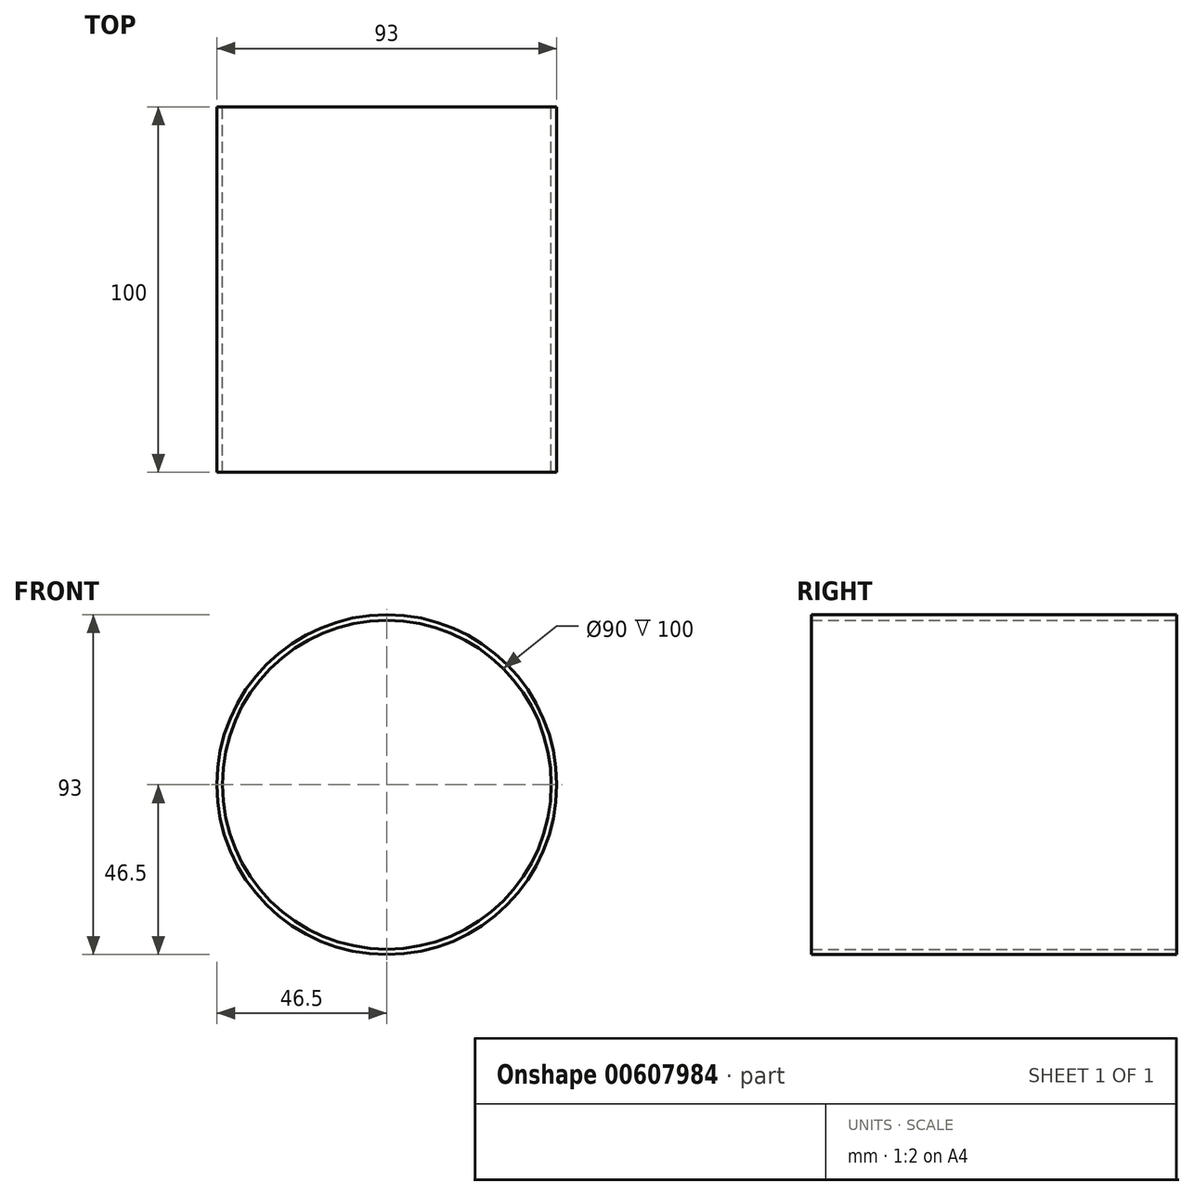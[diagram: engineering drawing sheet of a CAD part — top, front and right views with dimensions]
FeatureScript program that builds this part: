
annotation { "Feature Type Name" : "Feature", "Feature Type Description" : "" }
export const myFeature = defineFeature(function(context is Context, id is Id, definition is map)
    precondition{}
    {
        {
            var Q0;
            Q0=qCreatedBy(makeId("Front.planeOp"),FACE);
            var sketch = newSketch(context, id + "F0", { "sketchPlane" : qUnion([Q0])});
            skCircle(sketch, "E0", {"center": v(0, 0) * mm, "radius": 45 * mm});
            skCircle(sketch, "E1", {"center": v(0, 0) * mm, "radius": 46.5 * mm});
            skSolve(sketch);
        }
        {
            var Q0;
            Q0=qSketchRegion(id+"F0",true);
            extrude(context, id + "F1", {"entities" : qUnion([Q0]), "depth" : 100 * mm, "offsetDistance" : 25 * mm});
        }
    });
